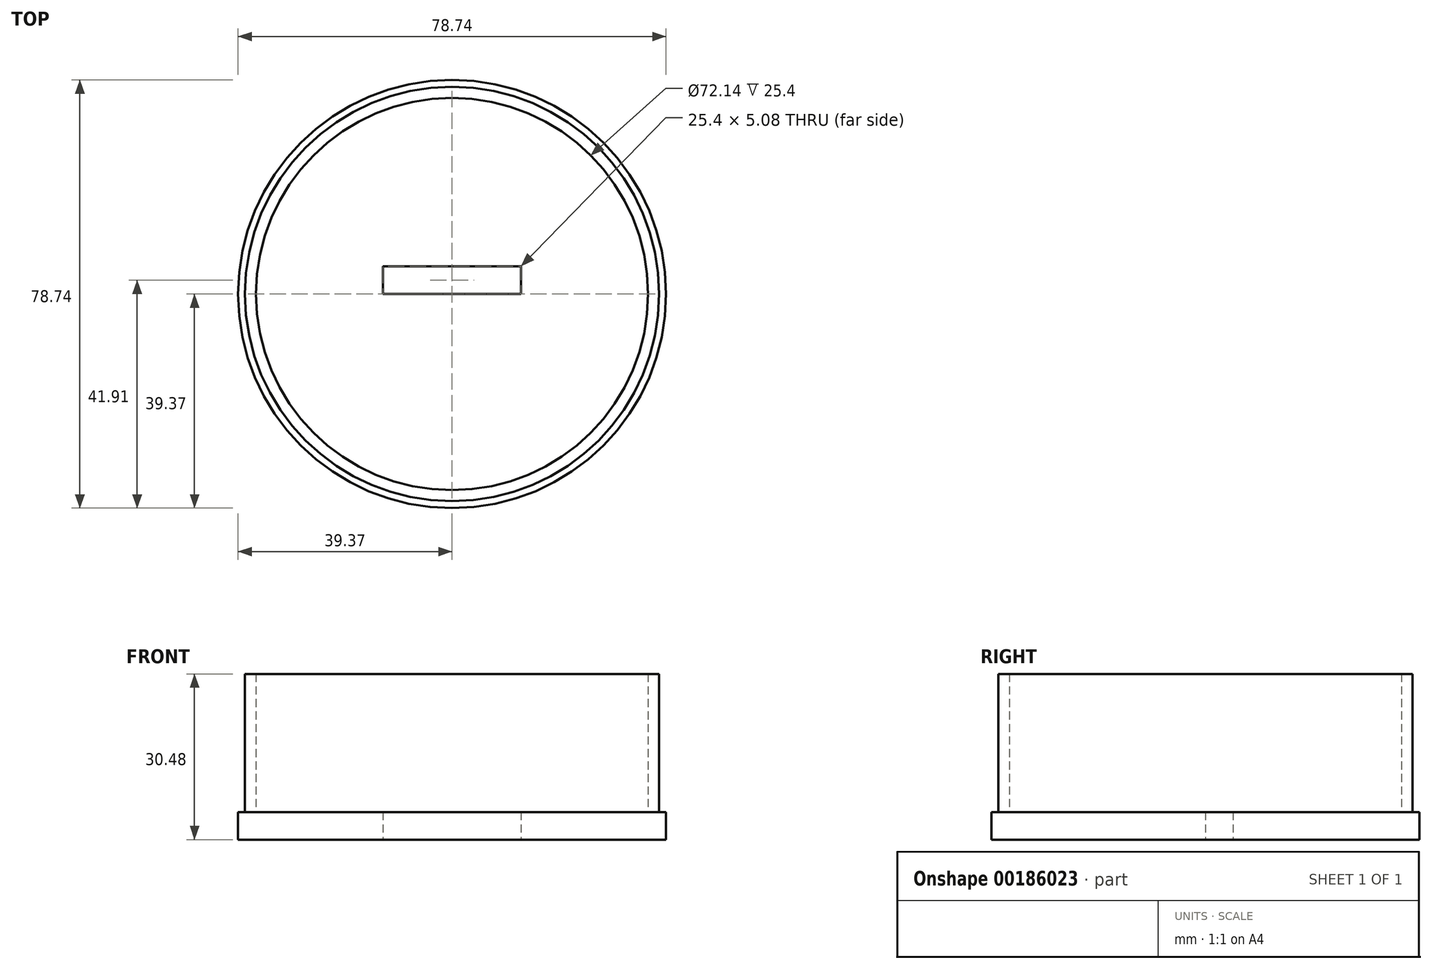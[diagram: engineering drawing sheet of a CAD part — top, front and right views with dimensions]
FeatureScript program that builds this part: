
annotation { "Feature Type Name" : "Feature", "Feature Type Description" : "" }
export const myFeature = defineFeature(function(context is Context, id is Id, definition is map)
    precondition{}
    {
        {
            var Q0;
            Q0=qCreatedBy(makeId("Top.planeOp"),FACE);
            var sketch = newSketch(context, id + "F0", { "sketchPlane" : qUnion([Q0])});
            skCircle(sketch, "E0", {"center": v(0, 0) * mm, "radius": 39.37 * mm});
            skSolve(sketch);
        }
        {
            var Q0;
            Q0=makeQuery(id+"F0.imprint","IMPRINT",FACE,{"disambiguationData":[TD([[makeQuery(id+"F0.imprint","IMPRINT",EDGE,{"derivedFrom":sQuery(id+"F0.wireOp",EDGE,"E0")}),1.0]])]});
            extrude(context, id + "F1", {"entities" : qUnion([Q0]), "depth" : 5.08 * mm});
        }
        {
            var Q0;
            Q0=makeQuery(id+"F1.opExtrude","CAP_FACE",FACE,{"disambiguationData":[OSD([sQuery(id+"F0.wireOp",EDGE,"E0")])],"isStart":false});
            var sketch = newSketch(context, id + "F2", { "sketchPlane" : qUnion([Q0])});
            skCircle(sketch, "E1", {"center": v(0, 0) * mm, "radius": 38.1 * mm});
            skCircle(sketch, "E2", {"center": v(0, 0) * mm, "radius": 36.07 * mm});
            skSolve(sketch);
        }
        {
            var Q0;
            Q0=makeQuery(id+"F2.imprint","IMPRINT",FACE,{"disambiguationData":[TD([[makeQuery(id+"F2.imprint","IMPRINT",EDGE,{"derivedFrom":sQuery(id+"F2.wireOp",EDGE,"E1")}),1.0]])]});
            extrude(context, id + "F3", {"entities" : qUnion([Q0]), "operationType" : NewBodyOperationType.ADD, "depth" : 25.4 * mm});
        }
        {
            var Q0;
            Q0=makeQuery(id+"F1.opExtrude","CAP_FACE",FACE,{"disambiguationData":[OSD([sQuery(id+"F0.wireOp",EDGE,"E0")])],"isStart":true});
            var sketch = newSketch(context, id + "F4", { "sketchPlane" : qUnion([Q0])});
            skLineSegment(sketch, "E3.bottom", {"start": v(-12.7, 0) * mm, "end": v(12.7, 0) * mm});
            skLineSegment(sketch, "E3.top", {"start": v(-12.7, -5.08) * mm, "end": v(12.7, -5.08) * mm});
            skLineSegment(sketch, "E3.left", {"start": v(-12.7, 0) * mm, "end": v(-12.7, -5.08) * mm});
            skLineSegment(sketch, "E3.right", {"start": v(12.7, 0) * mm, "end": v(12.7, -5.08) * mm});
            skSolve(sketch);
        }
        {
            var Q0;
            Q0=makeQuery(id+"F4.imprint","IMPRINT",FACE,{"disambiguationData":[TD([[makeQuery(id+"F4.imprint","IMPRINT",EDGE,{"derivedFrom":sQuery(id+"F4.wireOp",EDGE,"E3.bottom")}),-1.0]])]});
            extrude(context, id + "F5", {"entities" : qUnion([Q0]), "operationType" : NewBodyOperationType.REMOVE, "oppositeDirection" : true, "depth" : 5.08 * mm});
        }
    });
